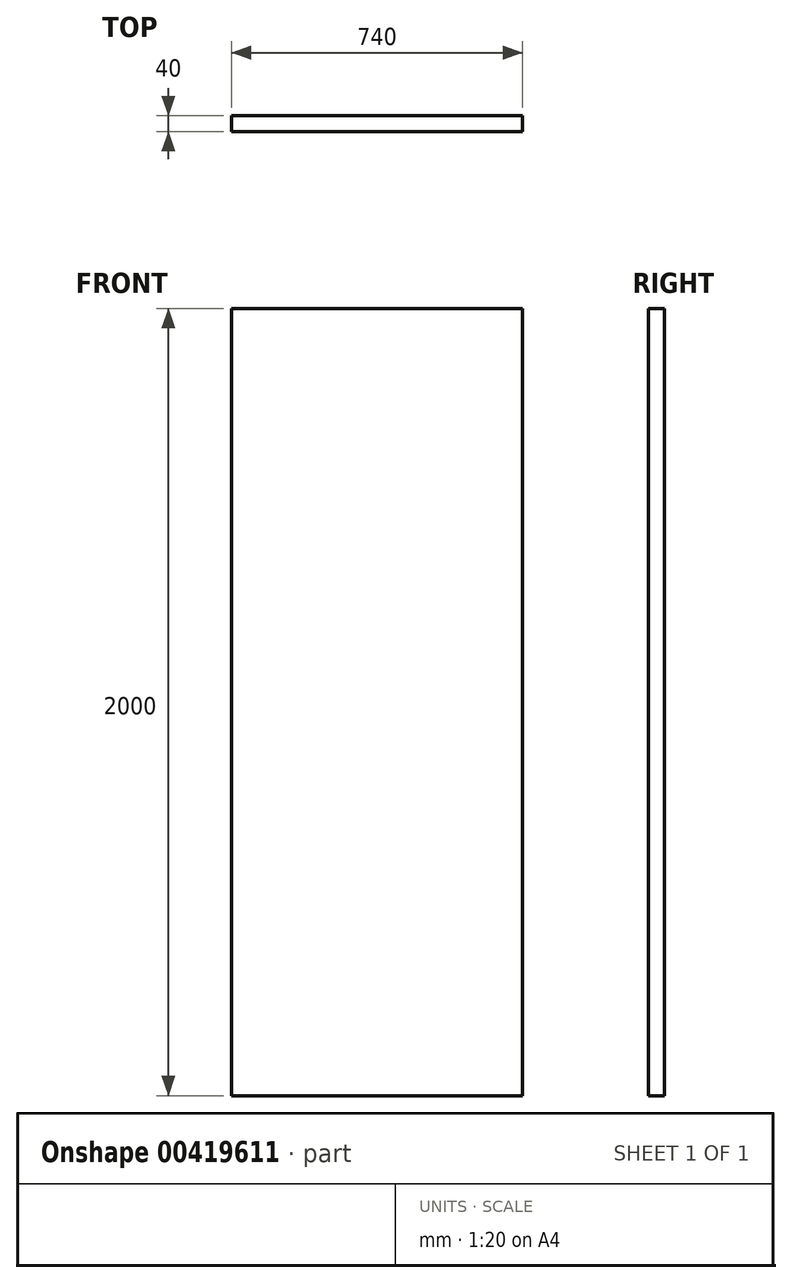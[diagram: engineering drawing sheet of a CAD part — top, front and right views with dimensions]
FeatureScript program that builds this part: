
annotation { "Feature Type Name" : "Feature", "Feature Type Description" : "" }
export const myFeature = defineFeature(function(context is Context, id is Id, definition is map)
    precondition{}
    {
        {
            var Q0;
            Q0=qCreatedBy(makeId("Top.planeOp"),FACE);
            var sketch = newSketch(context, id + "F0", { "sketchPlane" : qUnion([Q0])});
            skLineSegment(sketch, "E0.bottom", {"start": v(-624, -6.93) * mm, "end": v(116, -6.93) * mm});
            skLineSegment(sketch, "E0.top", {"start": v(-624, -46.93) * mm, "end": v(116, -46.93) * mm});
            skLineSegment(sketch, "E0.left", {"start": v(-624, -6.93) * mm, "end": v(-624, -46.93) * mm});
            skLineSegment(sketch, "E0.right", {"start": v(116, -6.93) * mm, "end": v(116, -46.93) * mm});
            skSolve(sketch);
        }
        {
            var Q0;
            Q0=makeQuery(id+"F0.imprint","IMPRINT",FACE,{"disambiguationData":[TD([[makeQuery(id+"F0.imprint","IMPRINT",EDGE,{"derivedFrom":sQuery(id+"F0.wireOp",EDGE,"E0.bottom")}),-1.0]])]});
            extrude(context, id + "F1", {"entities" : qUnion([Q0]), "depth" : 2000 * mm});
        }
    });
